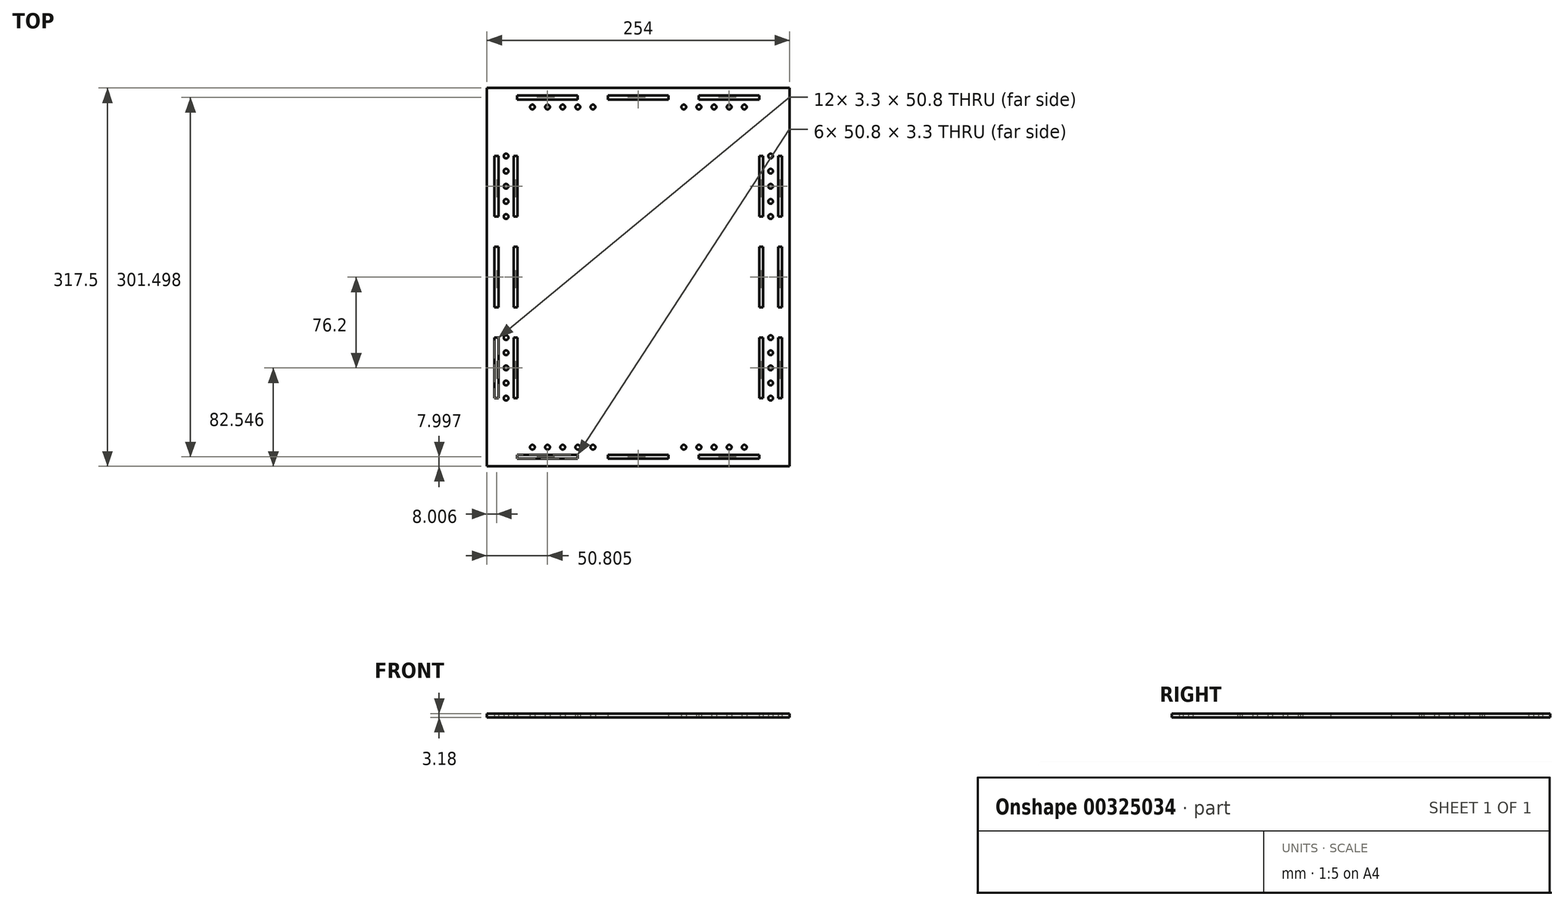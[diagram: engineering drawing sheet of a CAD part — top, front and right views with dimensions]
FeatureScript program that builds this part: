
annotation { "Feature Type Name" : "Feature", "Feature Type Description" : "" }
export const myFeature = defineFeature(function(context is Context, id is Id, definition is map)
    precondition{}
    {
        {
            var Q0;
            Q0=qCreatedBy(makeId("Top.planeOp"),FACE);
            var sketch = newSketch(context, id + "F0", { "sketchPlane" : qUnion([Q0])});
            skLineSegment(sketch, "E0.bottom", {"start": v(130.42, -167.2) * mm, "end": v(-123.58, -167.2) * mm});
            skLineSegment(sketch, "E0.top", {"start": v(130.42, 150.3) * mm, "end": v(-123.58, 150.3) * mm});
            skLineSegment(sketch, "E0.left", {"start": v(130.42, -167.2) * mm, "end": v(130.42, 150.3) * mm});
            skLineSegment(sketch, "E0.right", {"start": v(-123.58, -167.2) * mm, "end": v(-123.58, 150.3) * mm});
            skPoint(sketch, "E0.middle", {"position": v(3.42, -8.44) * mm});
            skLineSegment(sketch, "E1.bottom", {"start": v(-98.18, 143.96) * mm, "end": v(-47.38, 143.96) * mm});
            skLineSegment(sketch, "E1.top", {"start": v(-98.18, 140.65) * mm, "end": v(-47.38, 140.65) * mm});
            skLineSegment(sketch, "E1.left", {"start": v(-98.18, 143.96) * mm, "end": v(-98.18, 140.65) * mm});
            skLineSegment(sketch, "E1.right", {"start": v(-47.38, 143.96) * mm, "end": v(-47.38, 140.65) * mm});
            skLineSegment(sketch, "E2.bottom", {"start": v(-21.98, 143.96) * mm, "end": v(28.82, 143.96) * mm});
            skLineSegment(sketch, "E2.top", {"start": v(-21.98, 140.65) * mm, "end": v(28.82, 140.65) * mm});
            skLineSegment(sketch, "E2.left", {"start": v(-21.98, 143.96) * mm, "end": v(-21.98, 140.65) * mm});
            skLineSegment(sketch, "E2.right", {"start": v(28.82, 143.96) * mm, "end": v(28.82, 140.65) * mm});
            skLineSegment(sketch, "E3", {"start": v(-47.38, 143.96) * mm, "end": v(-21.98, 143.96) * mm, "construction": true});
            skLineSegment(sketch, "E4", {"start": v(-98.18, 143.96) * mm, "end": v(-123.58, 143.96) * mm, "construction": true});
            skLineSegment(sketch, "E5.MirrorCS", {"start": v(105.02, 140.65) * mm, "end": v(54.22, 140.65) * mm});
            skLineSegment(sketch, "E6.MirrorCS", {"start": v(105.02, 143.96) * mm, "end": v(54.22, 143.96) * mm});
            skLineSegment(sketch, "E7.MirrorCS", {"start": v(54.22, 143.96) * mm, "end": v(54.22, 140.65) * mm});
            skLineSegment(sketch, "E8.MirrorCS", {"start": v(105.02, 143.96) * mm, "end": v(105.02, 140.65) * mm});
            skLineSegment(sketch, "E9.MirrorCS", {"start": v(-47.38, -160.84) * mm, "end": v(-47.38, -157.54) * mm});
            skLineSegment(sketch, "E10.MirrorCS", {"start": v(-21.98, -157.54) * mm, "end": v(28.82, -157.54) * mm});
            skLineSegment(sketch, "E11.MirrorCS", {"start": v(28.82, -160.84) * mm, "end": v(28.82, -157.54) * mm});
            skLineSegment(sketch, "E12.MirrorCS", {"start": v(105.02, -157.54) * mm, "end": v(54.22, -157.54) * mm});
            skLineSegment(sketch, "E13.MirrorCS", {"start": v(54.22, -160.84) * mm, "end": v(54.22, -157.54) * mm});
            skLineSegment(sketch, "E14.MirrorCS", {"start": v(-98.18, -157.54) * mm, "end": v(-47.38, -157.54) * mm});
            skLineSegment(sketch, "E15.MirrorCS", {"start": v(105.02, -160.84) * mm, "end": v(105.02, -157.54) * mm});
            skLineSegment(sketch, "E16.MirrorCS", {"start": v(-21.98, -160.84) * mm, "end": v(-21.98, -157.54) * mm});
            skLineSegment(sketch, "E17.MirrorCS", {"start": v(105.02, -160.84) * mm, "end": v(54.22, -160.84) * mm});
            skLineSegment(sketch, "E18.MirrorCS", {"start": v(-21.98, -160.84) * mm, "end": v(28.82, -160.84) * mm});
            skLineSegment(sketch, "E19.MirrorCS", {"start": v(-47.38, -160.84) * mm, "end": v(-21.98, -160.84) * mm, "construction": true});
            skLineSegment(sketch, "E20.MirrorCS", {"start": v(-98.18, -160.84) * mm, "end": v(-47.38, -160.84) * mm});
            skLineSegment(sketch, "E21.MirrorCS", {"start": v(-98.18, -160.84) * mm, "end": v(-98.18, -157.54) * mm});
            skLineSegment(sketch, "E22.bottom", {"start": v(-117.23, 93.16) * mm, "end": v(-113.92, 93.16) * mm});
            skLineSegment(sketch, "E22.top", {"start": v(-117.23, 42.36) * mm, "end": v(-113.92, 42.36) * mm});
            skLineSegment(sketch, "E22.left", {"start": v(-117.23, 93.16) * mm, "end": v(-117.23, 42.36) * mm});
            skLineSegment(sketch, "E22.right", {"start": v(-113.92, 93.16) * mm, "end": v(-113.92, 42.36) * mm});
            skLineSegment(sketch, "E23.0.1.0", {"start": v(-113.92, 16.96) * mm, "end": v(-113.92, -33.84) * mm});
            skLineSegment(sketch, "E23.0.1.1", {"start": v(-117.23, 16.96) * mm, "end": v(-117.23, -33.84) * mm});
            skLineSegment(sketch, "E23.0.1.2", {"start": v(-117.23, 16.96) * mm, "end": v(-113.92, 16.96) * mm});
            skLineSegment(sketch, "E23.0.1.3", {"start": v(-117.23, -33.84) * mm, "end": v(-113.92, -33.84) * mm});
            skLineSegment(sketch, "E23.0.2.0", {"start": v(-113.92, -59.24) * mm, "end": v(-113.92, -110.04) * mm});
            skLineSegment(sketch, "E23.0.2.1", {"start": v(-117.23, -59.24) * mm, "end": v(-117.23, -110.04) * mm});
            skLineSegment(sketch, "E23.0.2.2", {"start": v(-117.23, -59.24) * mm, "end": v(-113.92, -59.24) * mm});
            skLineSegment(sketch, "E23.0.2.3", {"start": v(-117.23, -110.04) * mm, "end": v(-113.92, -110.04) * mm});
            skLineSegment(sketch, "E23.direction1", {"start": v(-117.23, 42.36) * mm, "end": v(-101.22, 42.36) * mm, "construction": true});
            skLineSegment(sketch, "E23.direction2", {"start": v(-117.23, 42.36) * mm, "end": v(-117.23, -33.84) * mm, "construction": true});
            skLineSegment(sketch, "E24.MirrorCS", {"start": v(120.77, 16.96) * mm, "end": v(120.77, -33.84) * mm});
            skLineSegment(sketch, "E25.MirrorCS", {"start": v(124.07, -59.24) * mm, "end": v(120.77, -59.24) * mm});
            skLineSegment(sketch, "E26.MirrorCS", {"start": v(124.07, 16.96) * mm, "end": v(124.07, -33.84) * mm});
            skLineSegment(sketch, "E27.MirrorCS", {"start": v(124.07, -110.04) * mm, "end": v(120.77, -110.04) * mm});
            skLineSegment(sketch, "E28.MirrorCS", {"start": v(124.07, 16.96) * mm, "end": v(120.77, 16.96) * mm});
            skLineSegment(sketch, "E29.MirrorCS", {"start": v(124.07, -33.84) * mm, "end": v(120.77, -33.84) * mm});
            skLineSegment(sketch, "E30.MirrorCS", {"start": v(124.07, 42.36) * mm, "end": v(124.07, -33.84) * mm, "construction": true});
            skLineSegment(sketch, "E31.MirrorCS", {"start": v(124.07, 93.16) * mm, "end": v(120.77, 93.16) * mm});
            skLineSegment(sketch, "E32.MirrorCS", {"start": v(124.07, 42.36) * mm, "end": v(120.77, 42.36) * mm});
            skLineSegment(sketch, "E33.MirrorCS", {"start": v(124.07, 93.16) * mm, "end": v(124.07, 42.36) * mm});
            skLineSegment(sketch, "E34.MirrorCS", {"start": v(120.77, -59.24) * mm, "end": v(120.77, -110.04) * mm});
            skLineSegment(sketch, "E35.MirrorCS", {"start": v(120.77, 93.16) * mm, "end": v(120.77, 42.36) * mm});
            skLineSegment(sketch, "E36.MirrorCS", {"start": v(124.07, -59.24) * mm, "end": v(124.07, -110.04) * mm});
            skLineSegment(sketch, "E37.0.1.0", {"start": v(-97.92, 93.16) * mm, "end": v(-97.92, 42.36) * mm});
            skLineSegment(sketch, "E37.3.1.0", {"start": v(-101.22, 93.16) * mm, "end": v(-101.22, 42.36) * mm});
            skLineSegment(sketch, "E37.6.1.0", {"start": v(-101.22, 93.16) * mm, "end": v(-97.92, 93.16) * mm});
            skLineSegment(sketch, "E37.9.1.0", {"start": v(-101.22, 42.36) * mm, "end": v(-97.92, 42.36) * mm});
            skLineSegment(sketch, "E37.0.1.1", {"start": v(-97.92, 16.96) * mm, "end": v(-97.92, -33.84) * mm});
            skLineSegment(sketch, "E37.3.1.1", {"start": v(-101.22, 16.96) * mm, "end": v(-101.22, -33.84) * mm});
            skLineSegment(sketch, "E37.6.1.1", {"start": v(-101.22, 16.96) * mm, "end": v(-97.92, 16.96) * mm});
            skLineSegment(sketch, "E37.9.1.1", {"start": v(-101.22, -33.84) * mm, "end": v(-97.92, -33.84) * mm});
            skLineSegment(sketch, "E37.0.1.2", {"start": v(-97.92, -59.24) * mm, "end": v(-97.92, -110.04) * mm});
            skLineSegment(sketch, "E37.3.1.2", {"start": v(-101.22, -59.24) * mm, "end": v(-101.22, -110.04) * mm});
            skLineSegment(sketch, "E37.6.1.2", {"start": v(-101.22, -59.24) * mm, "end": v(-97.92, -59.24) * mm});
            skLineSegment(sketch, "E37.9.1.2", {"start": v(-101.22, -110.04) * mm, "end": v(-97.92, -110.04) * mm});
            skLineSegment(sketch, "E38.MirrorCS", {"start": v(108.07, 93.16) * mm, "end": v(108.07, 42.36) * mm});
            skLineSegment(sketch, "E39.MirrorCS", {"start": v(108.07, 93.16) * mm, "end": v(104.77, 93.16) * mm});
            skLineSegment(sketch, "E40.MirrorCS", {"start": v(108.07, 42.36) * mm, "end": v(104.77, 42.36) * mm});
            skLineSegment(sketch, "E41.MirrorCS", {"start": v(108.07, -59.24) * mm, "end": v(108.07, -110.04) * mm});
            skLineSegment(sketch, "E42.MirrorCS", {"start": v(104.77, 16.96) * mm, "end": v(104.77, -33.84) * mm});
            skLineSegment(sketch, "E43.MirrorCS", {"start": v(108.07, -59.24) * mm, "end": v(104.77, -59.24) * mm});
            skLineSegment(sketch, "E44.MirrorCS", {"start": v(108.07, 16.96) * mm, "end": v(108.07, -33.84) * mm});
            skLineSegment(sketch, "E45.MirrorCS", {"start": v(108.07, -110.04) * mm, "end": v(104.77, -110.04) * mm});
            skLineSegment(sketch, "E46.MirrorCS", {"start": v(108.07, 16.96) * mm, "end": v(104.77, 16.96) * mm});
            skLineSegment(sketch, "E47.MirrorCS", {"start": v(108.07, -33.84) * mm, "end": v(104.77, -33.84) * mm});
            skLineSegment(sketch, "E48.MirrorCS", {"start": v(104.77, 93.16) * mm, "end": v(104.77, 42.36) * mm});
            skLineSegment(sketch, "E49.MirrorCS", {"start": v(104.77, -59.24) * mm, "end": v(104.77, -110.04) * mm});
            skLineSegment(sketch, "E50", {"start": v(-113.92, -84.64) * mm, "end": v(-101.22, -84.64) * mm, "construction": true});
            skLineSegment(sketch, "E51", {"start": v(-113.92, 67.76) * mm, "end": v(-101.22, 67.76) * mm, "construction": true});
            skLineSegment(sketch, "E52", {"start": v(-107.57, -84.64) * mm, "end": v(-107.57, -110.04) * mm, "construction": true});
            skLineSegment(sketch, "E53", {"start": v(-107.57, 67.76) * mm, "end": v(-107.57, 93.16) * mm, "construction": true});
            skCircle(sketch, "E54", {"center": v(-107.57, -59.24) * mm, "radius": 1.98 * mm});
            skCircle(sketch, "E55", {"center": v(-107.57, -71.94) * mm, "radius": 1.98 * mm});
            skCircle(sketch, "E56", {"center": v(-107.57, -84.64) * mm, "radius": 1.98 * mm});
            skCircle(sketch, "E57", {"center": v(-107.57, -97.34) * mm, "radius": 1.98 * mm});
            skCircle(sketch, "E58", {"center": v(-107.57, -110.04) * mm, "radius": 1.98 * mm});
            skCircle(sketch, "E59", {"center": v(-107.57, 42.36) * mm, "radius": 1.98 * mm});
            skCircle(sketch, "E60", {"center": v(-107.57, 67.76) * mm, "radius": 1.98 * mm});
            skCircle(sketch, "E61", {"center": v(-107.57, 80.46) * mm, "radius": 1.98 * mm});
            skCircle(sketch, "E62", {"center": v(-107.57, 93.16) * mm, "radius": 1.98 * mm});
            skCircle(sketch, "E63", {"center": v(-107.57, 55.06) * mm, "radius": 1.98 * mm});
            skLineSegment(sketch, "E64", {"start": v(3.42, -157.54) * mm, "end": v(3.42, 140.65) * mm, "construction": true});
            skCircle(sketch, "E65.MirrorC", {"center": v(114.42, -84.64) * mm, "radius": 1.98 * mm});
            skCircle(sketch, "E66.MirrorC", {"center": v(114.42, -97.34) * mm, "radius": 1.98 * mm});
            skCircle(sketch, "E67.MirrorC", {"center": v(114.42, 67.76) * mm, "radius": 1.98 * mm});
            skCircle(sketch, "E68.MirrorC", {"center": v(114.42, -110.04) * mm, "radius": 1.98 * mm});
            skCircle(sketch, "E69.MirrorC", {"center": v(114.42, 55.06) * mm, "radius": 1.98 * mm});
            skCircle(sketch, "E70.MirrorC", {"center": v(114.42, 42.36) * mm, "radius": 1.98 * mm});
            skLineSegment(sketch, "E71.MirrorCS", {"start": v(114.42, -84.64) * mm, "end": v(114.42, -110.04) * mm, "construction": true});
            skCircle(sketch, "E72.MirrorC", {"center": v(114.42, -71.94) * mm, "radius": 1.98 * mm});
            skLineSegment(sketch, "E73.MirrorCS", {"start": v(114.42, 67.76) * mm, "end": v(114.42, 93.16) * mm, "construction": true});
            skCircle(sketch, "E74.MirrorC", {"center": v(114.42, 80.46) * mm, "radius": 1.98 * mm});
            skCircle(sketch, "E75.MirrorC", {"center": v(114.42, -59.24) * mm, "radius": 1.98 * mm});
            skCircle(sketch, "E76.MirrorC", {"center": v(114.42, 93.16) * mm, "radius": 1.98 * mm});
            skLineSegment(sketch, "E77", {"start": v(-123.58, -151.2) * mm, "end": v(130.42, -151.2) * mm, "construction": true});
            skCircle(sketch, "E78", {"center": v(-72.78, -151.2) * mm, "radius": 1.98 * mm});
            skCircle(sketch, "E79", {"center": v(-60.08, -151.2) * mm, "radius": 1.98 * mm});
            skCircle(sketch, "E80", {"center": v(-47.38, -151.2) * mm, "radius": 1.98 * mm});
            skCircle(sketch, "E81", {"center": v(-34.68, -151.2) * mm, "radius": 1.98 * mm});
            skCircle(sketch, "E82", {"center": v(-85.48, -151.2) * mm, "radius": 1.98 * mm});
            skCircle(sketch, "E83", {"center": v(41.52, -151.2) * mm, "radius": 1.98 * mm});
            skCircle(sketch, "E84", {"center": v(54.22, -151.2) * mm, "radius": 1.98 * mm});
            skCircle(sketch, "E85", {"center": v(66.92, -151.2) * mm, "radius": 1.98 * mm});
            skCircle(sketch, "E86", {"center": v(79.62, -151.2) * mm, "radius": 1.98 * mm});
            skCircle(sketch, "E87", {"center": v(92.32, -151.2) * mm, "radius": 1.98 * mm});
            skLineSegment(sketch, "E88", {"start": v(3.42, -8.44) * mm, "end": v(-27.26, -8.44) * mm, "construction": true});
            skCircle(sketch, "E89.MirrorC", {"center": v(-47.38, 134.3) * mm, "radius": 1.98 * mm});
            skCircle(sketch, "E90.MirrorC", {"center": v(-60.08, 134.3) * mm, "radius": 1.98 * mm});
            skCircle(sketch, "E91.MirrorC", {"center": v(92.32, 134.3) * mm, "radius": 1.98 * mm});
            skCircle(sketch, "E92.MirrorC", {"center": v(-34.68, 134.3) * mm, "radius": 1.98 * mm});
            skCircle(sketch, "E93.MirrorC", {"center": v(-72.78, 134.3) * mm, "radius": 1.98 * mm});
            skCircle(sketch, "E94.MirrorC", {"center": v(-85.48, 134.3) * mm, "radius": 1.98 * mm});
            skCircle(sketch, "E95.MirrorC", {"center": v(54.22, 134.3) * mm, "radius": 1.98 * mm});
            skCircle(sketch, "E96.MirrorC", {"center": v(79.62, 134.3) * mm, "radius": 1.98 * mm});
            skCircle(sketch, "E97.MirrorC", {"center": v(41.52, 134.3) * mm, "radius": 1.98 * mm});
            skCircle(sketch, "E98.MirrorC", {"center": v(66.92, 134.3) * mm, "radius": 1.98 * mm});
            skSolve(sketch);
        }
        {
            var Q0;
            Q0=makeQuery(id+"F0.imprint","IMPRINT",FACE,{"disambiguationData":[TD([[makeQuery(id+"F0.imprint","IMPRINT",EDGE,{"derivedFrom":sQuery(id+"F0.wireOp",EDGE,"E0.bottom")}),-1.0]])]});
            extrude(context, id + "F1", {"entities" : qUnion([Q0]), "depth" : 3.17 * mm});
        }
    });
